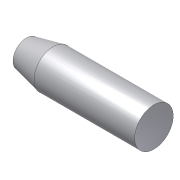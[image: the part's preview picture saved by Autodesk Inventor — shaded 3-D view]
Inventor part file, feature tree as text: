
AUTODESK INVENTOR PART (.ipt)
format: ipt  version: 2012 (Build 160160000, 160)  size: 75,264 bytes
history: native  units: in
note: dims shown in document units (in); Inventor stores cm internally (conversion verified against a paired STEP export)
features: revolve x1, sketch x1
ambient origin geometry x8: Origin, YZ Plane, XZ Plane, XY Plane, X Axis, Y Axis, Z Axis, Center Point
bodies: Solid1 (feature_tree)
feature tree (2):
  revolve  "Revolution1"  [1 undecoded]
  sketch  "Sketch1"  dims[d0=0.7188in d1=1.0in d2=0.5in d3=4.75in d4=90.0deg]
note: 1 required parameter value undecoded (feature->parameter linkage not recoverable at this tier; creation-order binding heuristic only, values carry confidence <= 0.55)
